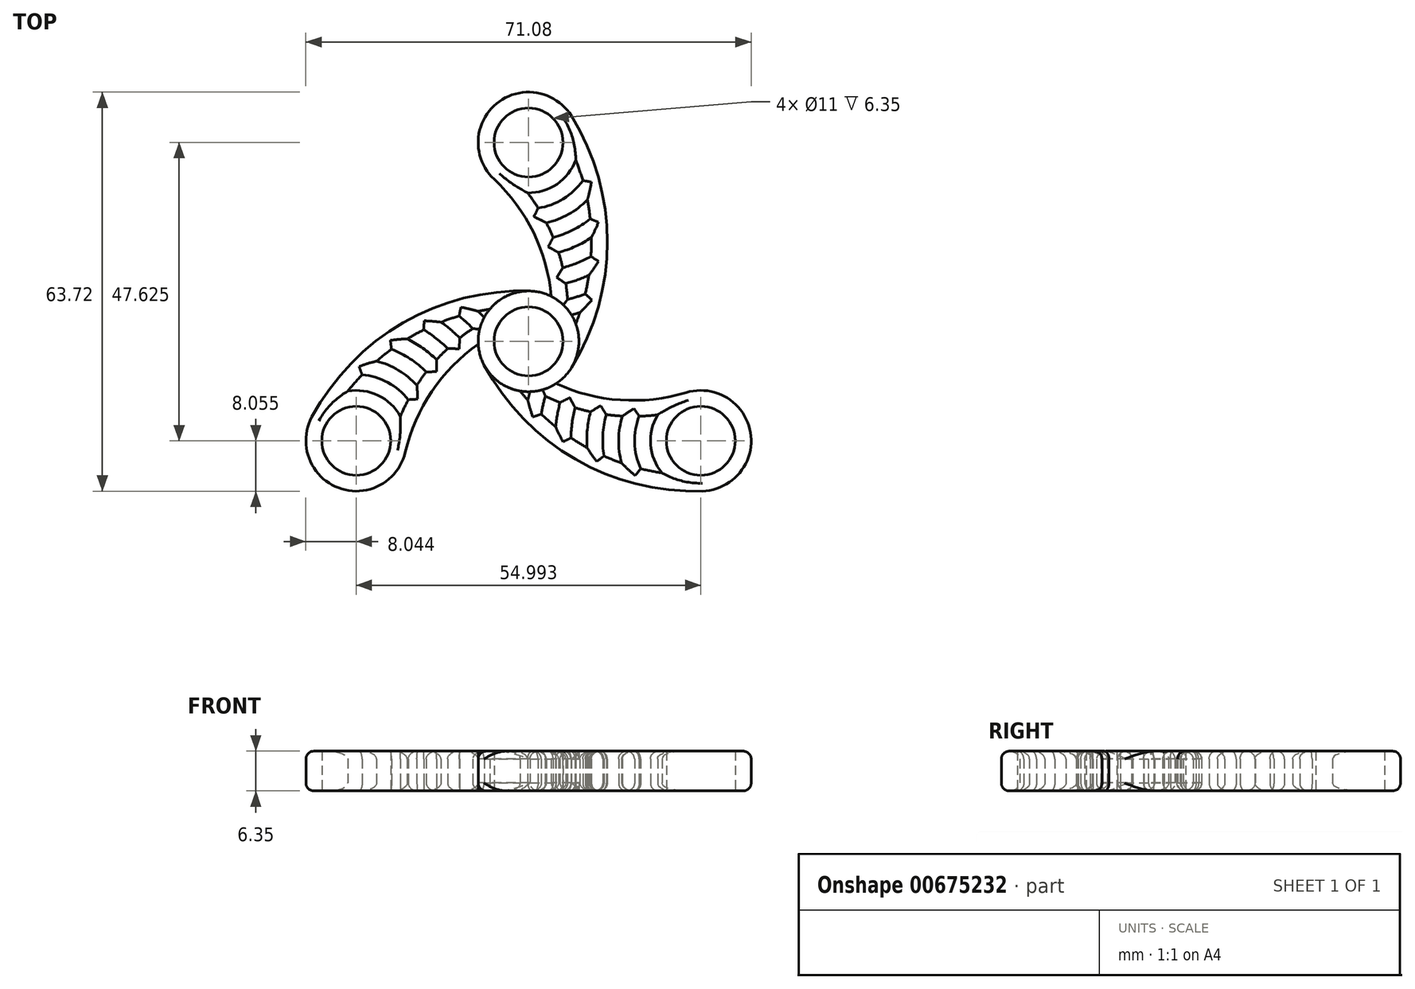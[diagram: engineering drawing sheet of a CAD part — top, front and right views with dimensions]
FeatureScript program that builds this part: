
annotation { "Feature Type Name" : "Feature", "Feature Type Description" : "" }
export const myFeature = defineFeature(function(context is Context, id is Id, definition is map)
    precondition{}
    {
        {
            var Q0;
            Q0=qCreatedBy(makeId("Top.planeOp"),FACE);
            var sketch = newSketch(context, id + "F0", { "sketchPlane" : qUnion([Q0])});
            skCircle(sketch, "E0", {"center": v(0, 0) * mm, "radius": 5.5 * mm});
            skArc(sketch, "E1", {"start": v(-0.14, 23.71) * mm, "mid": v(4.54, 25.11) * mm, "end": v(7.54, 28.96) * mm});
            skCircle(sketch, "E2", {"center": v(0, 31.75) * mm, "radius": 5.5 * mm});
            skLineSegment(sketch, "E3", {"start": v(0, 0) * mm, "end": v(0, 31.75) * mm, "construction": true});
            skArc(sketch, "E4", {"start": v(6.83, -4.25) * mm, "mid": v(12.57, 15.87) * mm, "end": v(6.83, 36) * mm});
            skArc(sketch, "E5", {"start": v(3.64, 7.17) * mm, "mid": v(0.79, 17.37) * mm, "end": v(-5.5, 25.88) * mm});
            skArc(sketch, "E6", {"start": v(6.22, 6.7) * mm, "mid": v(6.1, 7.97) * mm, "end": v(5.94, 9.24) * mm});
            skArc(sketch, "E7", {"start": v(7.54, 2.8) * mm, "mid": v(7.88, 3.7) * mm, "end": v(8.2, 4.6) * mm});
            skLineSegment(sketch, "E8", {"start": v(-26.24, 0) * mm, "end": v(26.73, 0) * mm, "construction": true});
            skArc(sketch, "E9.trimOffspring", {"start": v(3.64, 7.17) * mm, "mid": v(-7.74, -2.16) * mm, "end": v(6.83, -4.25) * mm});
            skArc(sketch, "E10.trimOffspring", {"start": v(7.54, 2.8) * mm, "mid": v(7.23, 3.53) * mm, "end": v(6.84, 4.23) * mm});
            skArc(sketch, "E11.trimOffspring", {"start": v(6.83, 36) * mm, "mid": v(-5.1, 37.97) * mm, "end": v(-5.5, 25.88) * mm});
            skArc(sketch, "E12", {"start": v(1.53, 21.28) * mm, "mid": v(5.54, 22.74) * mm, "end": v(8.66, 25.67) * mm});
            skArc(sketch, "E13", {"start": v(2.84, 18.94) * mm, "mid": v(6.38, 20.29) * mm, "end": v(9.4, 22.6) * mm});
            skArc(sketch, "E14", {"start": v(3.92, 16.59) * mm, "mid": v(7.04, 17.76) * mm, "end": v(9.84, 19.57) * mm});
            skArc(sketch, "E15", {"start": v(4.8, 14.2) * mm, "mid": v(7.5, 15.17) * mm, "end": v(10.03, 16.56) * mm});
            skArc(sketch, "E16", {"start": v(5.47, 11.74) * mm, "mid": v(7.77, 12.52) * mm, "end": v(9.96, 13.56) * mm});
            skArc(sketch, "E17", {"start": v(5.94, 9.24) * mm, "mid": v(7.82, 9.82) * mm, "end": v(9.63, 10.56) * mm});
            skArc(sketch, "E18", {"start": v(6.22, 6.7) * mm, "mid": v(7.65, 7.09) * mm, "end": v(9.05, 7.57) * mm});
            skArc(sketch, "E19", {"start": v(6.84, 4.23) * mm, "mid": v(7.52, 4.4) * mm, "end": v(8.2, 4.6) * mm});
            skArc(sketch, "E20.trimOffspring", {"start": v(8.66, 25.67) * mm, "mid": v(8.14, 27.33) * mm, "end": v(7.54, 28.96) * mm});
            skArc(sketch, "E21.trimOffspring", {"start": v(1.53, 21.28) * mm, "mid": v(0.72, 22.52) * mm, "end": v(-0.14, 23.71) * mm});
            skArc(sketch, "E22.trimOffspring", {"start": v(9.84, 19.57) * mm, "mid": v(9.65, 21.08) * mm, "end": v(9.4, 22.6) * mm});
            skArc(sketch, "E23.trimOffspring", {"start": v(3.92, 16.59) * mm, "mid": v(3.4, 17.78) * mm, "end": v(2.84, 18.94) * mm});
            skArc(sketch, "E24.trimOffspring", {"start": v(9.96, 13.56) * mm, "mid": v(10.02, 15.06) * mm, "end": v(10.03, 16.56) * mm});
            skArc(sketch, "E25.trimOffspring", {"start": v(9.05, 7.57) * mm, "mid": v(9.37, 9.06) * mm, "end": v(9.63, 10.56) * mm});
            skArc(sketch, "E26.trimOffspring", {"start": v(5.47, 11.74) * mm, "mid": v(5.15, 12.97) * mm, "end": v(4.8, 14.2) * mm});
            skPoint(sketch, "E27.orphan", {"position": v(6.3, 5) * mm});
            skArc(sketch, "E28", {"start": v(6.83, -4.25) * mm, "mid": v(7.74, 2.16) * mm, "end": v(3.64, 7.17) * mm});
            skSolve(sketch);
        }
        {
            var Q0;
            Q0=makeQuery(id+"F0.imprint","IMPRINT",FACE,{"disambiguationData":[TD([[makeQuery(id+"F0.imprint","IMPRINT",EDGE,{"derivedFrom":sQuery(id+"F0.wireOp",EDGE,"E0")}),-1.0]])]});
            extrude(context, id + "F1", {"entities" : qUnion([Q0]), "depth" : 6.35 * mm, "offsetDistance" : 25.4 * mm});
        }
        {
            var Q0;
            {var subQ0=sQuery(id+"F0.wireOp",EDGE,"E28");var subQ1=sQuery(id+"F0.wireOp",EDGE,"E9.trimOffspring");Q0=makeQuery(id+"F6.boolean.opBoolean","SPLIT",EDGE,{"disambiguationData":[TD([makeQuery(id+"F1.opExtrude","CAP_FACE",FACE,{"disambiguationData":[OSD([sQuery(id+"F0.wireOp",EDGE,"E0"),subQ1,subQ0])],"isStart":true}),makeQuery(id+"F1.opExtrude","SWEPT_FACE",FACE,{"disambiguationData":[OSD([subQ1,subQ0])]}),makeQuery(id+"F5.opFillet","BLEND_FACE",FACE,{"disambiguationData":[OSD([sQuery(id+"F0.wireOp",EDGE,"E6")])]}),makeQuery(id+"F6.opPattern","COPY",FACE,{"derivedFrom":makeQuery(id+"F5.opFillet","BLEND_FACE",FACE,{"disambiguationData":[OSD([sQuery(id+"F0.wireOp",EDGE,"E20.trimOffspring")])]}),"instanceName":"1"})])],"derivedFrom":makeQuery(id+"F1.opExtrude","CAP_EDGE",EDGE,{"disambiguationData":[OSD([subQ1,subQ0])],"isStart":true})});}
            var Q1;
            Q1=makeQuery(id+"F1.opExtrude","CAP_EDGE",EDGE,{"disambiguationData":[OSD([sQuery(id+"F0.wireOp",EDGE,"E9.trimOffspring"),sQuery(id+"F0.wireOp",EDGE,"E28")])],"isStart":false});
            fillet(context, id + "F2", {"entities" : qUnion([Q0, Q1]), "radius" : 1.27 * mm, "tangentPropagation" : true, "allowEdgeOverflow" : false});
        }
        {
            var Q0;
            Q0=makeQuery(id+"F0.imprint","IMPRINT",FACE,{"disambiguationData":[TD([[makeQuery(id+"F0.imprint","IMPRINT",EDGE,{"derivedFrom":sQuery(id+"F0.wireOp",EDGE,"E1")}),1.0]])]});
            extrude(context, id + "F3", {"entities" : qUnion([Q0]), "depth" : 6.35 * mm, "offsetDistance" : 25.4 * mm});
        }
        {
            var Q0;
            Q0=makeQuery(id+"F1.opExtrude","CAP_EDGE",EDGE,{"disambiguationData":[OSD([sQuery(id+"F0.wireOp",EDGE,"bpce36zP-iXU5-sNKe-X4ck-L7L7D1vI4rVC")])],"isStart":false});
            var Q1;
            Q1=makeQuery(id+"F1.opExtrude","CAP_EDGE",EDGE,{"disambiguationData":[OSD([sQuery(id+"F0.wireOp",EDGE,"e7503e0b-2cf4-4764-9a25-7df3317fb831.trimOffspring")])],"isStart":false});
            var Q2;
            Q2=makeQuery(id+"F1.opExtrude","CAP_EDGE",EDGE,{"disambiguationData":[OSD([sQuery(id+"F0.wireOp",EDGE,"83012717-f670-44a8-b870-8f0312a39590.trimOffspring")])],"isStart":false});
            var Q3;
            Q3=makeQuery(id+"F1.opExtrude","CAP_EDGE",EDGE,{"disambiguationData":[OSD([sQuery(id+"F0.wireOp",EDGE,"9630bcc3-2082-418c-bbc4-93741d624b1e.trimOffspring")])],"isStart":false});
            var Q4;
            Q4=makeQuery(id+"F1.opExtrude","CAP_EDGE",EDGE,{"disambiguationData":[OSD([sQuery(id+"F0.wireOp",EDGE,"8uJXmObA-TCDu-9xxq-OS8d-51lf73224O7t")])],"isStart":false});
            var Q5;
            Q5=makeQuery(id+"F1.opExtrude","CAP_EDGE",EDGE,{"disambiguationData":[OSD([sQuery(id+"F0.wireOp",EDGE,"mNJpuXuZ-SJLH-9J18-7krx-NJ6o2L9N8Epc")])],"isStart":false});
            var Q6;
            Q6=makeQuery(id+"F1.opExtrude","CAP_EDGE",EDGE,{"disambiguationData":[OSD([sQuery(id+"F0.wireOp",EDGE,"GSR8SXzg-2xS6-zIou-HrmB-UwRTTvpV7Y7l")])],"isStart":false});
            var Q7;
            Q7=makeQuery(id+"F1.opExtrude","CAP_EDGE",EDGE,{"disambiguationData":[OSD([sQuery(id+"F0.wireOp",EDGE,"CuoT8f5h-3UQ6-whDg-Z1PD-sTu4X4Mv6G7V")])],"isStart":false});
            var Q8;
            Q8=makeQuery(id+"F1.opExtrude","CAP_EDGE",EDGE,{"disambiguationData":[OSD([sQuery(id+"F0.wireOp",EDGE,"a0f36f2d-0c8d-4468-858c-c933ae283161.trimOffspring")])],"isStart":false});
            var Q9;
            Q9=makeQuery(id+"F1.opExtrude","CAP_EDGE",EDGE,{"disambiguationData":[OSD([sQuery(id+"F0.wireOp",EDGE,"C299BugO-OB0B-AfGP-9ctg-gVESZcoSqvRi")])],"isStart":false});
            var Q10;
            Q10=makeQuery(id+"F1.opExtrude","CAP_EDGE",EDGE,{"disambiguationData":[OSD([sQuery(id+"F0.wireOp",EDGE,"tXSZDLL7-F1Az-dZwu-hV0r-t5xzoxktBVt0")])],"isStart":false});
            var Q11;
            Q11=makeQuery(id+"F1.opExtrude","CAP_EDGE",EDGE,{"disambiguationData":[OSD([sQuery(id+"F0.wireOp",EDGE,"PRYdNTXZ-h7Kn-Vm1Q-kHFx-BGrTxntyRKVB")])],"isStart":false});
            var Q12;
            Q12=makeQuery(id+"F1.opExtrude","CAP_EDGE",EDGE,{"disambiguationData":[OSD([sQuery(id+"F0.wireOp",EDGE,"4e9390af-9ce9-4a83-a180-aa4e39f585c1.trimOffspring")])],"isStart":false});
            var Q13;
            Q13=makeQuery(id+"F1.opExtrude","CAP_EDGE",EDGE,{"disambiguationData":[OSD([sQuery(id+"F0.wireOp",EDGE,"DlMuWKOR-oXFB-tFB8-cNDU-idYFUf7SfUB9")])],"isStart":false});
            var Q14;
            Q14=makeQuery(id+"F1.opExtrude","CAP_EDGE",EDGE,{"disambiguationData":[OSD([sQuery(id+"F0.wireOp",EDGE,"DJvWBBNc-WMiN-gR23-oh6b-L3THaTZwiPhr")])],"isStart":false});
            var Q15;
            Q15=makeQuery(id+"F1.opExtrude","CAP_EDGE",EDGE,{"disambiguationData":[OSD([sQuery(id+"F0.wireOp",EDGE,"xRSnhAvL-NHb5-iTgw-S4iv-s29s9ZAATVdL")])],"isStart":false});
            var Q16;
            Q16=makeQuery(id+"F1.opExtrude","CAP_EDGE",EDGE,{"disambiguationData":[OSD([sQuery(id+"F0.wireOp",EDGE,"2239eecf-bef5-42e9-96f5-82d8706a383a.trimOffspring")])],"isStart":false});
            var Q17;
            Q17=makeQuery(id+"F1.opExtrude","CAP_EDGE",EDGE,{"disambiguationData":[OSD([sQuery(id+"F0.wireOp",EDGE,"b2264944-adee-4cb3-aae6-dfeb488c43b3.trimOffspring")])],"isStart":false});
            var Q18;
            Q18=makeQuery(id+"F1.opExtrude","CAP_EDGE",EDGE,{"disambiguationData":[OSD([sQuery(id+"F0.wireOp",EDGE,"7D5ddEes-JzrO-7KwP-nOrY-BNfQKunNfQQZ")])],"isStart":false});
            var Q19;
            Q19=makeQuery(id+"F1.opExtrude","CAP_EDGE",EDGE,{"disambiguationData":[OSD([sQuery(id+"F0.wireOp",EDGE,"f89c8141-4557-40d6-b0ae-eabd8c864643.trimOffspring")])],"isStart":false});
            var Q20;
            Q20=makeQuery(id+"F1.opExtrude","CAP_EDGE",EDGE,{"disambiguationData":[OSD([sQuery(id+"F0.wireOp",EDGE,"E18")])],"isStart":false});
            var Q21;
            Q21=makeQuery(id+"F1.opExtrude","CAP_EDGE",EDGE,{"disambiguationData":[OSD([sQuery(id+"F0.wireOp",EDGE,"E6")])],"isStart":false});
            var Q22;
            Q22=makeQuery(id+"F1.opExtrude","CAP_EDGE",EDGE,{"disambiguationData":[OSD([sQuery(id+"F0.wireOp",EDGE,"E17")])],"isStart":false});
            var Q23;
            Q23=makeQuery(id+"F1.opExtrude","CAP_EDGE",EDGE,{"disambiguationData":[OSD([sQuery(id+"F0.wireOp",EDGE,"E25.trimOffspring")])],"isStart":false});
            var Q24;
            Q24=makeQuery(id+"F1.opExtrude","CAP_EDGE",EDGE,{"disambiguationData":[OSD([sQuery(id+"F0.wireOp",EDGE,"E15")])],"isStart":false});
            var Q25;
            Q25=makeQuery(id+"F1.opExtrude","CAP_EDGE",EDGE,{"disambiguationData":[OSD([sQuery(id+"F0.wireOp",EDGE,"E26.trimOffspring")])],"isStart":false});
            var Q26;
            Q26=makeQuery(id+"F1.opExtrude","CAP_EDGE",EDGE,{"disambiguationData":[OSD([sQuery(id+"F0.wireOp",EDGE,"E16")])],"isStart":false});
            var Q27;
            Q27=makeQuery(id+"F1.opExtrude","CAP_EDGE",EDGE,{"disambiguationData":[OSD([sQuery(id+"F0.wireOp",EDGE,"E24.trimOffspring")])],"isStart":false});
            var Q28;
            Q28=makeQuery(id+"F1.opExtrude","CAP_EDGE",EDGE,{"disambiguationData":[OSD([sQuery(id+"F0.wireOp",EDGE,"E23.trimOffspring")])],"isStart":false});
            var Q29;
            Q29=makeQuery(id+"F1.opExtrude","CAP_EDGE",EDGE,{"disambiguationData":[OSD([sQuery(id+"F0.wireOp",EDGE,"E14")])],"isStart":false});
            var Q30;
            Q30=makeQuery(id+"F1.opExtrude","CAP_EDGE",EDGE,{"disambiguationData":[OSD([sQuery(id+"F0.wireOp",EDGE,"E13")])],"isStart":false});
            var Q31;
            Q31=makeQuery(id+"F1.opExtrude","CAP_EDGE",EDGE,{"disambiguationData":[OSD([sQuery(id+"F0.wireOp",EDGE,"E22.trimOffspring")])],"isStart":false});
            var Q32;
            Q32=makeQuery(id+"F1.opExtrude","CAP_EDGE",EDGE,{"disambiguationData":[OSD([sQuery(id+"F0.wireOp",EDGE,"E20.trimOffspring")])],"isStart":false});
            var Q33;
            Q33=makeQuery(id+"F1.opExtrude","CAP_EDGE",EDGE,{"disambiguationData":[OSD([sQuery(id+"F0.wireOp",EDGE,"E12")])],"isStart":false});
            var Q34;
            Q34=makeQuery(id+"F1.opExtrude","CAP_EDGE",EDGE,{"disambiguationData":[OSD([sQuery(id+"F0.wireOp",EDGE,"E1")])],"isStart":false});
            var Q35;
            Q35=makeQuery(id+"F1.opExtrude","CAP_EDGE",EDGE,{"disambiguationData":[OSD([sQuery(id+"F0.wireOp",EDGE,"E21.trimOffspring")])],"isStart":false});
            var Q36;
            Q36=makeQuery(id+"F1.opExtrude","CAP_EDGE",EDGE,{"disambiguationData":[OSD([sQuery(id+"F0.wireOp",EDGE,"E10.trimOffspring")])],"isStart":false});
            var Q37;
            Q37=makeQuery(id+"F1.opExtrude","CAP_EDGE",EDGE,{"disambiguationData":[OSD([sQuery(id+"F0.wireOp",EDGE,"E7")])],"isStart":false});
            var Q38;
            Q38=makeQuery(id+"F1.opExtrude","CAP_EDGE",EDGE,{"disambiguationData":[OSD([sQuery(id+"F0.wireOp",EDGE,"E19")])],"isStart":false});
            var Q39;
            Q39=makeQuery(id+"F3.opExtrude","CAP_EDGE",EDGE,{"disambiguationData":[OSD([sQuery(id+"F0.wireOp",EDGE,"E19")])],"isStart":false});
            var Q40;
            Q40=makeQuery(id+"F3.opExtrude","CAP_EDGE",EDGE,{"disambiguationData":[OSD([sQuery(id+"F0.wireOp",EDGE,"E7")])],"isStart":false});
            var Q41;
            Q41=makeQuery(id+"F3.opExtrude","CAP_EDGE",EDGE,{"disambiguationData":[OSD([sQuery(id+"F0.wireOp",EDGE,"E18")])],"isStart":false});
            var Q42;
            Q42=makeQuery(id+"F3.opExtrude","CAP_EDGE",EDGE,{"disambiguationData":[OSD([sQuery(id+"F0.wireOp",EDGE,"E17")])],"isStart":false});
            var Q43;
            Q43=makeQuery(id+"F3.opExtrude","CAP_EDGE",EDGE,{"disambiguationData":[OSD([sQuery(id+"F0.wireOp",EDGE,"E4")])],"isStart":false});
            var Q44;
            Q44=makeQuery(id+"F3.opExtrude","CAP_EDGE",EDGE,{"disambiguationData":[OSD([sQuery(id+"F0.wireOp",EDGE,"E15")])],"isStart":false});
            var Q45;
            Q45=makeQuery(id+"F3.opExtrude","CAP_EDGE",EDGE,{"disambiguationData":[OSD([sQuery(id+"F0.wireOp",EDGE,"E16")])],"isStart":false});
            var Q46;
            Q46=makeQuery(id+"F3.opExtrude","CAP_EDGE",EDGE,{"disambiguationData":[OSD([sQuery(id+"F0.wireOp",EDGE,"E26.trimOffspring")])],"isStart":false});
            var Q47;
            Q47=makeQuery(id+"F3.opExtrude","CAP_EDGE",EDGE,{"disambiguationData":[OSD([sQuery(id+"F0.wireOp",EDGE,"E24.trimOffspring")])],"isStart":false});
            var Q48;
            Q48=makeQuery(id+"F3.opExtrude","CAP_EDGE",EDGE,{"disambiguationData":[OSD([sQuery(id+"F0.wireOp",EDGE,"E25.trimOffspring")])],"isStart":false});
            var Q49;
            Q49=makeQuery(id+"F3.opExtrude","CAP_EDGE",EDGE,{"disambiguationData":[OSD([sQuery(id+"F0.wireOp",EDGE,"E6")])],"isStart":false});
            var Q50;
            Q50=makeQuery(id+"F3.opExtrude","CAP_EDGE",EDGE,{"disambiguationData":[OSD([sQuery(id+"F0.wireOp",EDGE,"E14")])],"isStart":false});
            var Q51;
            Q51=makeQuery(id+"F3.opExtrude","CAP_EDGE",EDGE,{"disambiguationData":[OSD([sQuery(id+"F0.wireOp",EDGE,"E13")])],"isStart":false});
            var Q52;
            Q52=makeQuery(id+"F3.opExtrude","CAP_EDGE",EDGE,{"disambiguationData":[OSD([sQuery(id+"F0.wireOp",EDGE,"E23.trimOffspring")])],"isStart":false});
            var Q53;
            Q53=makeQuery(id+"F3.opExtrude","CAP_EDGE",EDGE,{"disambiguationData":[OSD([sQuery(id+"F0.wireOp",EDGE,"E22.trimOffspring")])],"isStart":false});
            var Q54;
            Q54=makeQuery(id+"F3.opExtrude","CAP_EDGE",EDGE,{"disambiguationData":[OSD([sQuery(id+"F0.wireOp",EDGE,"E20.trimOffspring")])],"isStart":false});
            var Q55;
            Q55=makeQuery(id+"F3.opExtrude","CAP_EDGE",EDGE,{"disambiguationData":[OSD([sQuery(id+"F0.wireOp",EDGE,"E12")])],"isStart":false});
            var Q56;
            Q56=makeQuery(id+"F3.opExtrude","CAP_EDGE",EDGE,{"disambiguationData":[OSD([sQuery(id+"F0.wireOp",EDGE,"E21.trimOffspring")])],"isStart":false});
            var Q57;
            Q57=makeQuery(id+"F3.opExtrude","CAP_EDGE",EDGE,{"disambiguationData":[OSD([sQuery(id+"F0.wireOp",EDGE,"E1")])],"isStart":false});
            fillet(context, id + "F4", {"entities" : qUnion([Q0, Q1, Q2, Q3, Q4, Q5, Q6, Q7, Q8, Q9, Q10, Q11, Q12, Q13, Q14, Q15, Q16, Q17, Q18, Q19, Q20, Q21, Q22, Q23, Q24, Q25, Q26, Q27, Q28, Q29, Q30, Q31, Q32, Q33, Q34, Q35, Q36, Q37, Q38, Q39, Q40, Q41, Q42, Q43, Q44, Q45, Q46, Q47, Q48, Q49, Q50, Q51, Q52, Q53, Q54, Q55, Q56, Q57]), "radius" : 1.27 * mm, "tangentPropagation" : true, "allowEdgeOverflow" : false});
        }
        {
            var Q0;
            Q0=makeQuery(id+"F3.opExtrude","CAP_EDGE",EDGE,{"disambiguationData":[OSD([sQuery(id+"F0.wireOp",EDGE,"E4")])],"isStart":true});
            var Q1;
            Q1=makeQuery(id+"F3.opExtrude","CAP_EDGE",EDGE,{"disambiguationData":[OSD([sQuery(id+"F0.wireOp",EDGE,"E15")])],"isStart":true});
            var Q2;
            Q2=makeQuery(id+"F3.opExtrude","CAP_EDGE",EDGE,{"disambiguationData":[OSD([sQuery(id+"F0.wireOp",EDGE,"E16")])],"isStart":true});
            var Q3;
            Q3=makeQuery(id+"F3.opExtrude","CAP_EDGE",EDGE,{"disambiguationData":[OSD([sQuery(id+"F0.wireOp",EDGE,"E17")])],"isStart":true});
            var Q4;
            Q4=makeQuery(id+"F3.opExtrude","CAP_EDGE",EDGE,{"disambiguationData":[OSD([sQuery(id+"F0.wireOp",EDGE,"E18")])],"isStart":true});
            var Q5;
            Q5=makeQuery(id+"F3.opExtrude","CAP_EDGE",EDGE,{"disambiguationData":[OSD([sQuery(id+"F0.wireOp",EDGE,"E19")])],"isStart":true});
            var Q6;
            Q6=makeQuery(id+"F3.opExtrude","CAP_EDGE",EDGE,{"disambiguationData":[OSD([sQuery(id+"F0.wireOp",EDGE,"E7")])],"isStart":true});
            var Q7;
            Q7=makeQuery(id+"F3.opExtrude","CAP_EDGE",EDGE,{"disambiguationData":[OSD([sQuery(id+"F0.wireOp",EDGE,"E14")])],"isStart":true});
            var Q8;
            Q8=makeQuery(id+"F3.opExtrude","CAP_EDGE",EDGE,{"disambiguationData":[OSD([sQuery(id+"F0.wireOp",EDGE,"E13")])],"isStart":true});
            var Q9;
            Q9=makeQuery(id+"F3.opExtrude","CAP_EDGE",EDGE,{"disambiguationData":[OSD([sQuery(id+"F0.wireOp",EDGE,"E1")])],"isStart":true});
            var Q10;
            Q10=makeQuery(id+"F3.opExtrude","CAP_EDGE",EDGE,{"disambiguationData":[OSD([sQuery(id+"F0.wireOp",EDGE,"E12")])],"isStart":true});
            var Q11;
            Q11=makeQuery(id+"F3.opExtrude","CAP_EDGE",EDGE,{"disambiguationData":[OSD([sQuery(id+"F0.wireOp",EDGE,"E21.trimOffspring")])],"isStart":true});
            var Q12;
            Q12=makeQuery(id+"F3.opExtrude","CAP_EDGE",EDGE,{"disambiguationData":[OSD([sQuery(id+"F0.wireOp",EDGE,"E20.trimOffspring")])],"isStart":true});
            var Q13;
            Q13=makeQuery(id+"F3.opExtrude","CAP_EDGE",EDGE,{"disambiguationData":[OSD([sQuery(id+"F0.wireOp",EDGE,"E22.trimOffspring")])],"isStart":true});
            var Q14;
            Q14=makeQuery(id+"F3.opExtrude","CAP_EDGE",EDGE,{"disambiguationData":[OSD([sQuery(id+"F0.wireOp",EDGE,"E23.trimOffspring")])],"isStart":true});
            var Q15;
            Q15=makeQuery(id+"F3.opExtrude","CAP_EDGE",EDGE,{"disambiguationData":[OSD([sQuery(id+"F0.wireOp",EDGE,"E26.trimOffspring")])],"isStart":true});
            var Q16;
            Q16=makeQuery(id+"F3.opExtrude","CAP_EDGE",EDGE,{"disambiguationData":[OSD([sQuery(id+"F0.wireOp",EDGE,"E24.trimOffspring")])],"isStart":true});
            var Q17;
            Q17=makeQuery(id+"F3.opExtrude","CAP_EDGE",EDGE,{"disambiguationData":[OSD([sQuery(id+"F0.wireOp",EDGE,"E25.trimOffspring")])],"isStart":true});
            var Q18;
            Q18=makeQuery(id+"F3.opExtrude","CAP_EDGE",EDGE,{"disambiguationData":[OSD([sQuery(id+"F0.wireOp",EDGE,"E6")])],"isStart":true});
            fillet(context, id + "F5", {"entities" : qUnion([Q0, Q1, Q2, Q3, Q4, Q5, Q6, Q7, Q8, Q9, Q10, Q11, Q12, Q13, Q14, Q15, Q16, Q17, Q18]), "radius" : 1.27 * mm, "tangentPropagation" : true, "allowEdgeOverflow" : false});
        }
        {
            var Q0;
            Q0=makeQuery(id+"F3.opExtrude","SWEPT_BODY",BODY,{"disambiguationData":[OSD([sQuery(id+"F0.wireOp",EDGE,"E1"),sQuery(id+"F0.wireOp",EDGE,"E2"),sQuery(id+"F0.wireOp",EDGE,"E4"),sQuery(id+"F0.wireOp",EDGE,"E5"),sQuery(id+"F0.wireOp",EDGE,"E6"),sQuery(id+"F0.wireOp",EDGE,"E7"),sQuery(id+"F0.wireOp",EDGE,"E11.trimOffspring"),sQuery(id+"F0.wireOp",EDGE,"E12"),sQuery(id+"F0.wireOp",EDGE,"E13"),sQuery(id+"F0.wireOp",EDGE,"E14"),sQuery(id+"F0.wireOp",EDGE,"E15"),sQuery(id+"F0.wireOp",EDGE,"E16"),sQuery(id+"F0.wireOp",EDGE,"E17"),sQuery(id+"F0.wireOp",EDGE,"E18"),sQuery(id+"F0.wireOp",EDGE,"E19"),sQuery(id+"F0.wireOp",EDGE,"E20.trimOffspring"),sQuery(id+"F0.wireOp",EDGE,"E21.trimOffspring"),sQuery(id+"F0.wireOp",EDGE,"E22.trimOffspring"),sQuery(id+"F0.wireOp",EDGE,"E23.trimOffspring"),sQuery(id+"F0.wireOp",EDGE,"E24.trimOffspring"),sQuery(id+"F0.wireOp",EDGE,"E25.trimOffspring"),sQuery(id+"F0.wireOp",EDGE,"E26.trimOffspring"),sQuery(id+"F0.wireOp",EDGE,"E28")])]});
            var Q1;
            Q1=makeQuery(id+"F1.opExtrude","CAP_EDGE",EDGE,{"disambiguationData":[OSD([sQuery(id+"F0.wireOp",EDGE,"E0")])],"isStart":false});
            circularPattern(context, id + "F6", {"operationType" : NewBodyOperationType.ADD, "entities" : qUnion([Q0]), "axis" : qUnion([Q1]), "angle" : 360 * degree, "instanceCount" : 3, "equalSpace" : true});
        }
    });
